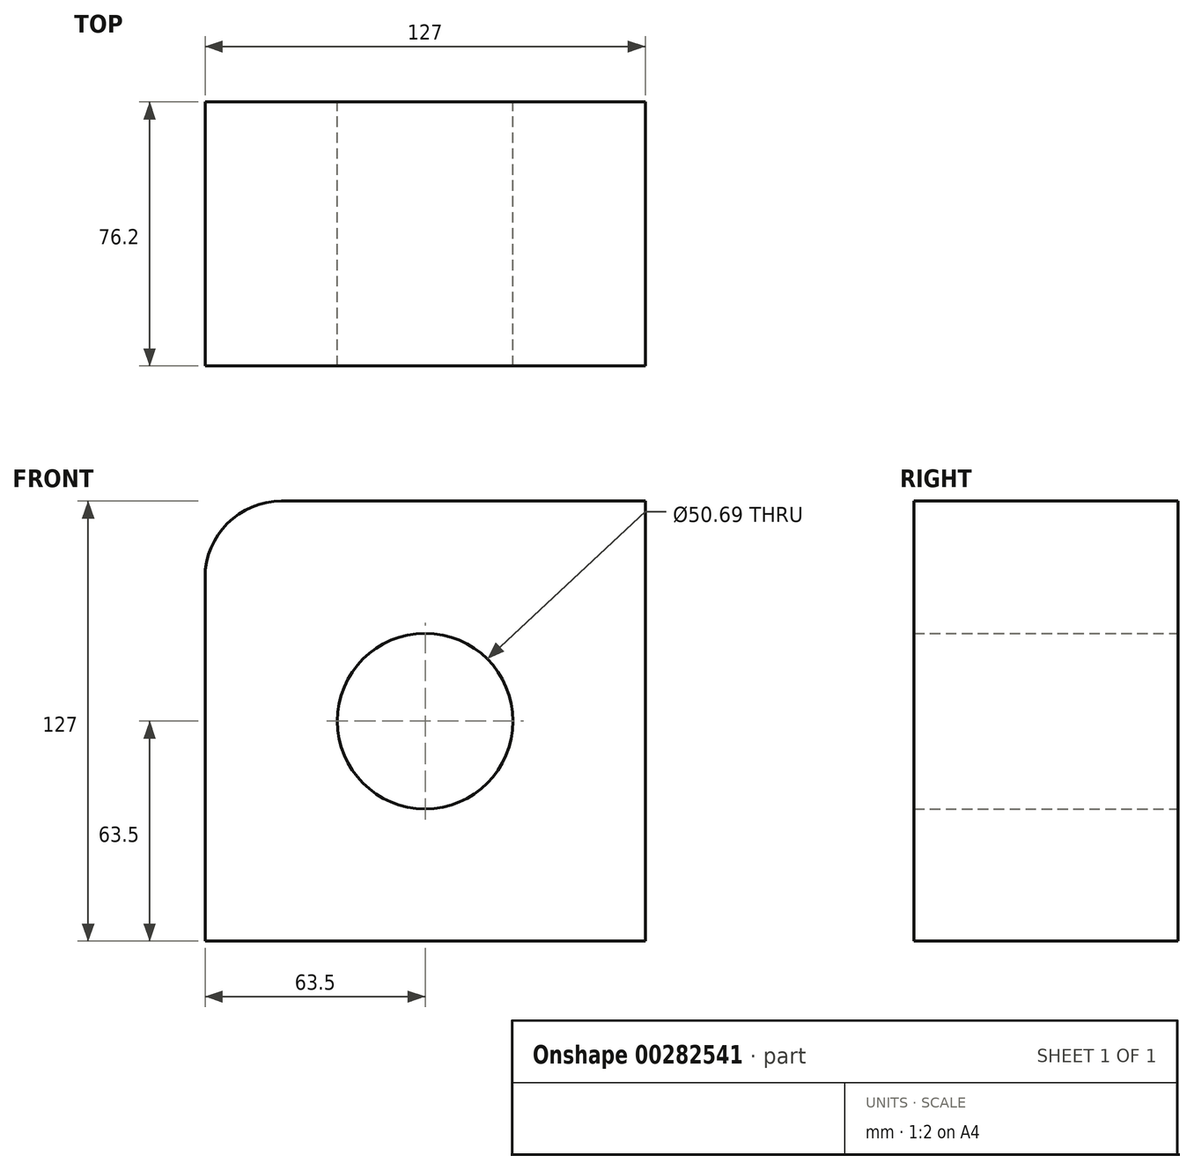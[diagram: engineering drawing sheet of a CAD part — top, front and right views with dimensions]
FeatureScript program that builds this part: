
annotation { "Feature Type Name" : "Feature", "Feature Type Description" : "" }
export const myFeature = defineFeature(function(context is Context, id is Id, definition is map)
    precondition{}
    {
        {
            var Q0;
            Q0=qCreatedBy(makeId("Top.planeOp"),FACE);
            var sketch = newSketch(context, id + "F0", { "sketchPlane" : qUnion([Q0])});
            skLineSegment(sketch, "E0.bottom", {"start": v(63.5, 38.1) * mm, "end": v(-63.5, 38.1) * mm});
            skLineSegment(sketch, "E0.top", {"start": v(63.5, -38.1) * mm, "end": v(-63.5, -38.1) * mm});
            skLineSegment(sketch, "E0.left", {"start": v(63.5, 38.1) * mm, "end": v(63.5, -38.1) * mm});
            skLineSegment(sketch, "E0.right", {"start": v(-63.5, 38.1) * mm, "end": v(-63.5, -38.1) * mm});
            skPoint(sketch, "E0.middle", {"position": v(0, 0) * mm});
            skSolve(sketch);
        }
        {
            var Q0;
            Q0=makeQuery(id+"F0.imprint","IMPRINT",FACE,{"disambiguationData":[TD([[makeQuery(id+"F0.imprint","IMPRINT",EDGE,{"derivedFrom":sQuery(id+"F0.wireOp",EDGE,"E0.bottom")}),1.0]])]});
            extrude(context, id + "F1", {"entities" : qUnion([Q0]), "endBound" : BoundingType.SYMMETRIC, "depth" : 127 * mm});
        }
        {
            var Q0;
            Q0=makeQuery(id+"F1.opExtrude","CAP_EDGE",EDGE,{"disambiguationData":[OSD([sQuery(id+"F0.wireOp",EDGE,"E0.right")])],"isStart":false});
            fillet(context, id + "F2", {"entities" : qUnion([Q0]), "radius" : 22.08 * mm, "tangentPropagation" : true, "allowEdgeOverflow" : false});
        }
        {
            var Q0;
            Q0=makeQuery(id+"F1.opExtrude","SWEPT_FACE",FACE,{"disambiguationData":[OSD([sQuery(id+"F0.wireOp",EDGE,"E0.bottom")])]});
            var sketch = newSketch(context, id + "F3", { "sketchPlane" : qUnion([Q0])});
            skCircle(sketch, "E1", {"center": v(0, 0) * mm, "radius": 25.35 * mm});
            skSolve(sketch);
        }
        {
            var Q0;
            Q0=makeQuery(id+"F3.imprint","IMPRINT",FACE,{"disambiguationData":[TD([[makeQuery(id+"F3.imprint","IMPRINT",EDGE,{"derivedFrom":sQuery(id+"F3.wireOp",EDGE,"E1")}),1.0]])]});
            extrude(context, id + "F4", {"entities" : qUnion([Q0]), "operationType" : NewBodyOperationType.REMOVE, "endBound" : BoundingType.THROUGH_ALL, "oppositeDirection" : true, "depth" : 25.4 * mm});
        }
    });
